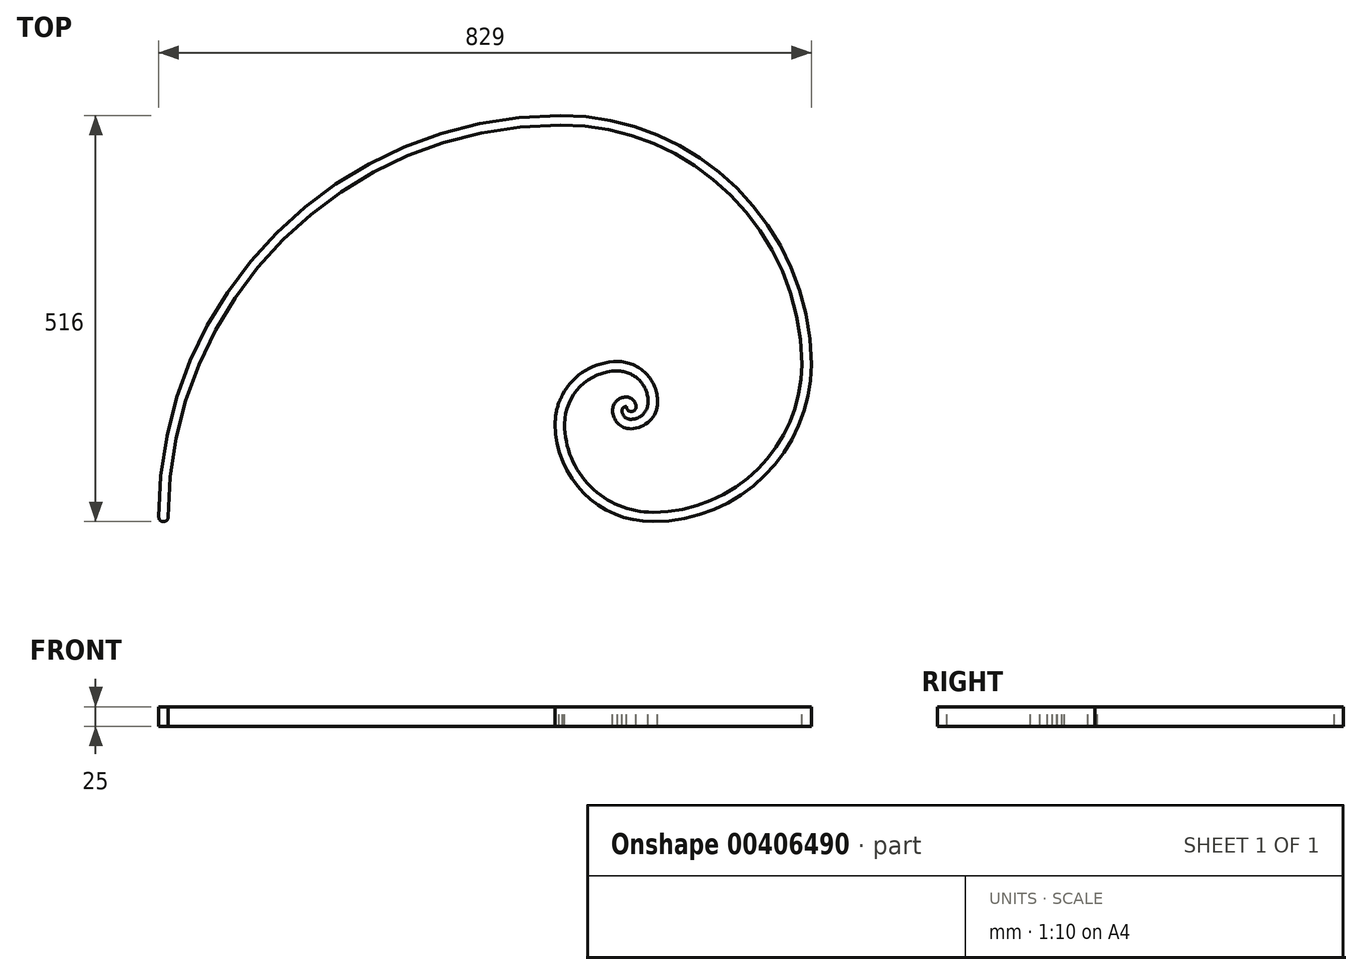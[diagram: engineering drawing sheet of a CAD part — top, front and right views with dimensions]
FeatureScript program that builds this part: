
annotation { "Feature Type Name" : "Feature", "Feature Type Description" : "" }
export const myFeature = defineFeature(function(context is Context, id is Id, definition is map)
    precondition{}
    {
        {
            var Q0;
            Q0=qCreatedBy(makeId("Top.planeOp"),FACE);
            var sketch = newSketch(context, id + "F0", { "sketchPlane" : qUnion([Q0])});
            skArc(sketch, "E0", {"start": v(-263.66, -263.17) * mm, "mid": v(-116.04, 93.21) * mm, "end": v(240.34, 240.83) * mm});
            skArc(sketch, "E1", {"start": v(240.34, 240.83) * mm, "mid": v(461.68, 149.15) * mm, "end": v(553.36, -72.19) * mm});
            skArc(sketch, "E2", {"start": v(553.35, -67.69) * mm, "mid": v(496.1, -205.91) * mm, "end": v(357.86, -263.17) * mm});
            skArc(sketch, "E3", {"start": v(357.87, -263.17) * mm, "mid": v(274.41, -228.6) * mm, "end": v(239.84, -145.14) * mm});
            skArc(sketch, "E4", {"start": v(239.84, -145.14) * mm, "mid": v(261.35, -93.2) * mm, "end": v(313.3, -71.69) * mm});
            skArc(sketch, "E5", {"start": v(312.8, -71.68) * mm, "mid": v(344.85, -85.06) * mm, "end": v(357.87, -117.27) * mm});
            skArc(sketch, "E6", {"start": v(357.87, -117.27) * mm, "mid": v(349.7, -136.97) * mm, "end": v(330, -145.14) * mm});
            skArc(sketch, "E7", {"start": v(330, -145.14) * mm, "mid": v(317.83, -140.1) * mm, "end": v(312.8, -127.93) * mm});
            skArc(sketch, "E8", {"start": v(312.8, -127.93) * mm, "mid": v(316.06, -120.04) * mm, "end": v(323.96, -116.77) * mm});
            skArc(sketch, "E9", {"start": v(323.96, -116.77) * mm, "mid": v(328.58, -118.68) * mm, "end": v(330.5, -123.3) * mm});
            skArc(sketch, "E10.0", {"start": v(323.96, -110.77) * mm, "mid": v(332.83, -114.44) * mm, "end": v(336.5, -123.3) * mm});
            skArc(sketch, "E10.1", {"start": v(306.8, -127.93) * mm, "mid": v(311.82, -115.8) * mm, "end": v(323.96, -110.77) * mm});
            skArc(sketch, "E10.2", {"start": v(330, -151.14) * mm, "mid": v(313.59, -144.34) * mm, "end": v(306.8, -127.93) * mm});
            skArc(sketch, "E10.3", {"start": v(363.87, -117.3) * mm, "mid": v(353.94, -141.23) * mm, "end": v(330, -151.14) * mm});
            skArc(sketch, "E10.4", {"start": v(313.3, -65.69) * mm, "mid": v(349.28, -81.01) * mm, "end": v(363.87, -117.3) * mm});
            skArc(sketch, "E10.5", {"start": v(233.84, -145.14) * mm, "mid": v(257.11, -88.96) * mm, "end": v(313.3, -65.69) * mm});
            skArc(sketch, "E10.6", {"start": v(-269.66, -263.17) * mm, "mid": v(-120.28, 97.46) * mm, "end": v(240.34, 246.83) * mm});
            skArc(sketch, "E10.7", {"start": v(240.34, 246.83) * mm, "mid": v(464.87, 154.44) * mm, "end": v(559.34, -69.22) * mm});
            skArc(sketch, "E10.8", {"start": v(559.34, -69.22) * mm, "mid": v(499.8, -210.7) * mm, "end": v(357.87, -269.17) * mm});
            skArc(sketch, "E10.9", {"start": v(357.87, -269.17) * mm, "mid": v(270.17, -232.84) * mm, "end": v(233.84, -145.14) * mm});
            skArc(sketch, "E11.0", {"start": v(323.96, -122.77) * mm, "mid": v(324.34, -122.92) * mm, "end": v(324.5, -123.3) * mm});
            skArc(sketch, "E11.1", {"start": v(318.8, -127.93) * mm, "mid": v(320.3, -124.28) * mm, "end": v(323.96, -122.77) * mm});
            skArc(sketch, "E11.2", {"start": v(330, -139.14) * mm, "mid": v(322.08, -135.85) * mm, "end": v(318.8, -127.93) * mm});
            skArc(sketch, "E11.3", {"start": v(351.87, -117.23) * mm, "mid": v(345.48, -132.72) * mm, "end": v(330, -139.14) * mm});
            skArc(sketch, "E11.4", {"start": v(313.23, -77.69) * mm, "mid": v(340.75, -89.45) * mm, "end": v(351.87, -117.23) * mm});
            skArc(sketch, "E11.5", {"start": v(245.84, -145.14) * mm, "mid": v(265.58, -97.46) * mm, "end": v(313.23, -77.69) * mm});
            skArc(sketch, "E11.6", {"start": v(-257.66, -263.17) * mm, "mid": v(-111.8, 88.97) * mm, "end": v(240.34, 234.83) * mm});
            skArc(sketch, "E11.7", {"start": v(240.34, 234.83) * mm, "mid": v(456.38, 145.95) * mm, "end": v(547.34, -69.22) * mm});
            skArc(sketch, "E11.8", {"start": v(547.34, -69.22) * mm, "mid": v(491.32, -202.2) * mm, "end": v(357.9, -257.17) * mm});
            skArc(sketch, "E11.9", {"start": v(357.9, -257.17) * mm, "mid": v(278.66, -224.36) * mm, "end": v(245.84, -145.14) * mm});
            skArc(sketch, "E12", {"start": v(336.5, -123.3) * mm, "mid": v(330.5, -129.3) * mm, "end": v(324.5, -123.3) * mm});
            skArc(sketch, "E13", {"start": v(-269.66, -263.17) * mm, "mid": v(-263.66, -269.17) * mm, "end": v(-257.66, -263.17) * mm});
            skLineSegment(sketch, "E14", {"start": v(-263.66, -269.17) * mm, "end": v(357.87, -269.17) * mm});
            skArc(sketch, "E15.MirrorCS", {"start": v(139.67, -258.93) * mm, "mid": v(198.42, -188.17) * mm, "end": v(243.16, -107.8) * mm});
            skArc(sketch, "E16.MirrorCS", {"start": v(148.16, -267.41) * mm, "mid": v(195.15, -213.3) * mm, "end": v(234.1, -153.12) * mm});
            skArc(sketch, "E17.MirrorCS", {"start": v(148.16, -267.41) * mm, "mid": v(139.67, -267.41) * mm, "end": v(139.67, -258.93) * mm});
            skLineSegment(sketch, "E18", {"start": v(143.92, -268.93) * mm, "end": v(143.92, -269.67) * mm});
            skSolve(sketch);
        }
        {
            var Q0;
            Q0=makeQuery(id+"F0.imprint","IMPRINT",FACE,{"disambiguationData":[TD([[makeQuery(id+"F0.imprint","IMPRINT",EDGE,{"derivedFrom":sQuery(id+"F0.wireOp",EDGE,"E10.0")}),1.0]])]});
            extrude(context, id + "F1", {"entities" : qUnion([Q0]), "depth" : -25 * mm});
        }
    });
